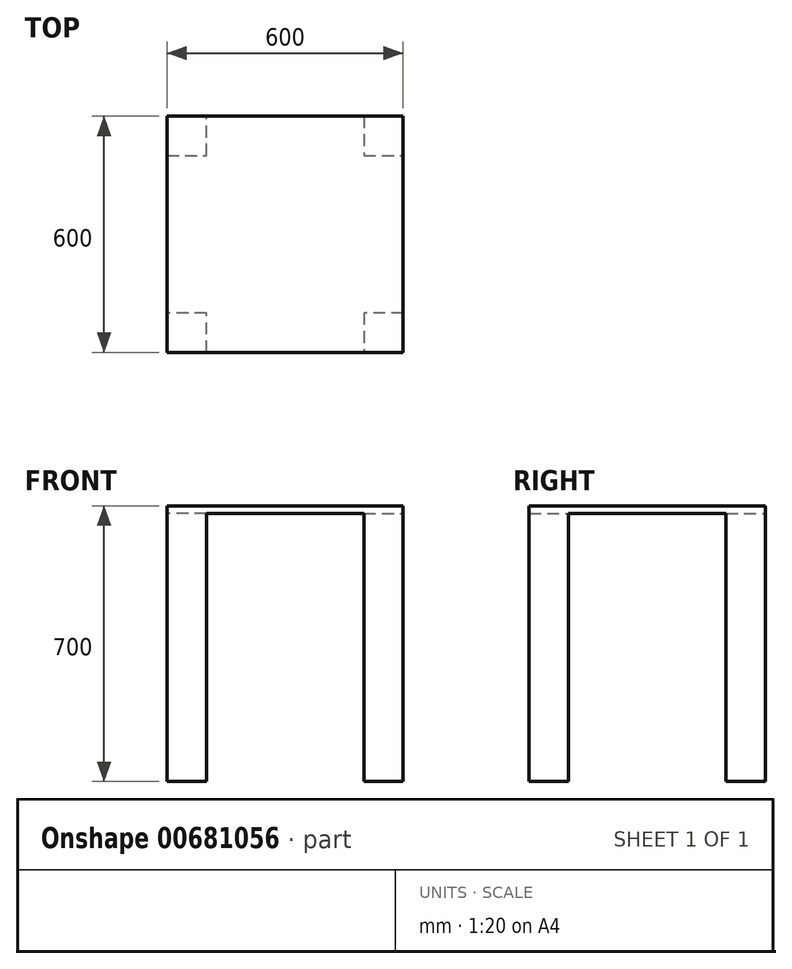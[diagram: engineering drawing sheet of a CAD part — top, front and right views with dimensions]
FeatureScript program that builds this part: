
annotation { "Feature Type Name" : "Feature", "Feature Type Description" : "" }
export const myFeature = defineFeature(function(context is Context, id is Id, definition is map)
    precondition{}
    {
        {
            var Q0;
            Q0=qCreatedBy(makeId("Top.planeOp"),FACE);
            var sketch = newSketch(context, id + "F0", { "sketchPlane" : qUnion([Q0])});
            skLineSegment(sketch, "E0.bottom", {"start": v(0, 0) * mm, "end": v(600, 0) * mm});
            skLineSegment(sketch, "E0.top", {"start": v(0, 600) * mm, "end": v(600, 600) * mm});
            skLineSegment(sketch, "E0.left", {"start": v(0, 0) * mm, "end": v(0, 600) * mm});
            skLineSegment(sketch, "E0.right", {"start": v(600, 0) * mm, "end": v(600, 600) * mm});
            skSolve(sketch);
        }
        {
            var Q0;
            Q0 = qSketchRegion(id + "F0", true);
            extrude(context, id + "F1", {"entities" : qUnion([Q0]), "depth" : 700 * mm, "offsetDistance" : 25 * mm});
        }
        {
            var Q0;
            Q0=makeQuery(id+"F1.opExtrude","CAP_FACE",FACE,{"disambiguationData":[OSD([sQuery(id+"F0.wireOp",EDGE,"E0.bottom"),sQuery(id+"F0.wireOp",EDGE,"E0.top"),sQuery(id+"F0.wireOp",EDGE,"E0.left"),sQuery(id+"F0.wireOp",EDGE,"E0.right")])],"isStart":true});
            var sketch = newSketch(context, id + "F2", { "sketchPlane" : qUnion([Q0])});
            skLineSegment(sketch, "E1", {"start": v(100, 0) * mm, "end": v(100, -100) * mm});
            skLineSegment(sketch, "E2", {"start": v(100, -100) * mm, "end": v(0, -100) * mm});
            skLineSegment(sketch, "E3", {"start": v(0, -100) * mm, "end": v(0, -500) * mm});
            skLineSegment(sketch, "E4", {"start": v(0, -500) * mm, "end": v(100, -500) * mm});
            skLineSegment(sketch, "E5", {"start": v(100, -500) * mm, "end": v(100, -600) * mm});
            skLineSegment(sketch, "E6", {"start": v(100, -600) * mm, "end": v(500, -600) * mm});
            skLineSegment(sketch, "E7", {"start": v(500, -600) * mm, "end": v(500, -500) * mm});
            skLineSegment(sketch, "E8", {"start": v(500, -500) * mm, "end": v(600, -500) * mm});
            skLineSegment(sketch, "E9", {"start": v(600, -500) * mm, "end": v(600, -100) * mm});
            skLineSegment(sketch, "E10", {"start": v(600, -100) * mm, "end": v(500, -100) * mm});
            skLineSegment(sketch, "E11", {"start": v(500, -100) * mm, "end": v(500, 0) * mm});
            skLineSegment(sketch, "E12", {"start": v(500, 0) * mm, "end": v(100, 0) * mm});
            skSolve(sketch);
        }
        {
            var Q0;
            Q0 = qSketchRegion(id + "F2", true);
            extrude(context, id + "F3", {"entities" : qUnion([Q0]), "operationType" : NewBodyOperationType.REMOVE, "oppositeDirection" : true, "depth" : (700 - 20) * mm, "offsetDistance" : 25 * mm});
        }
    });
